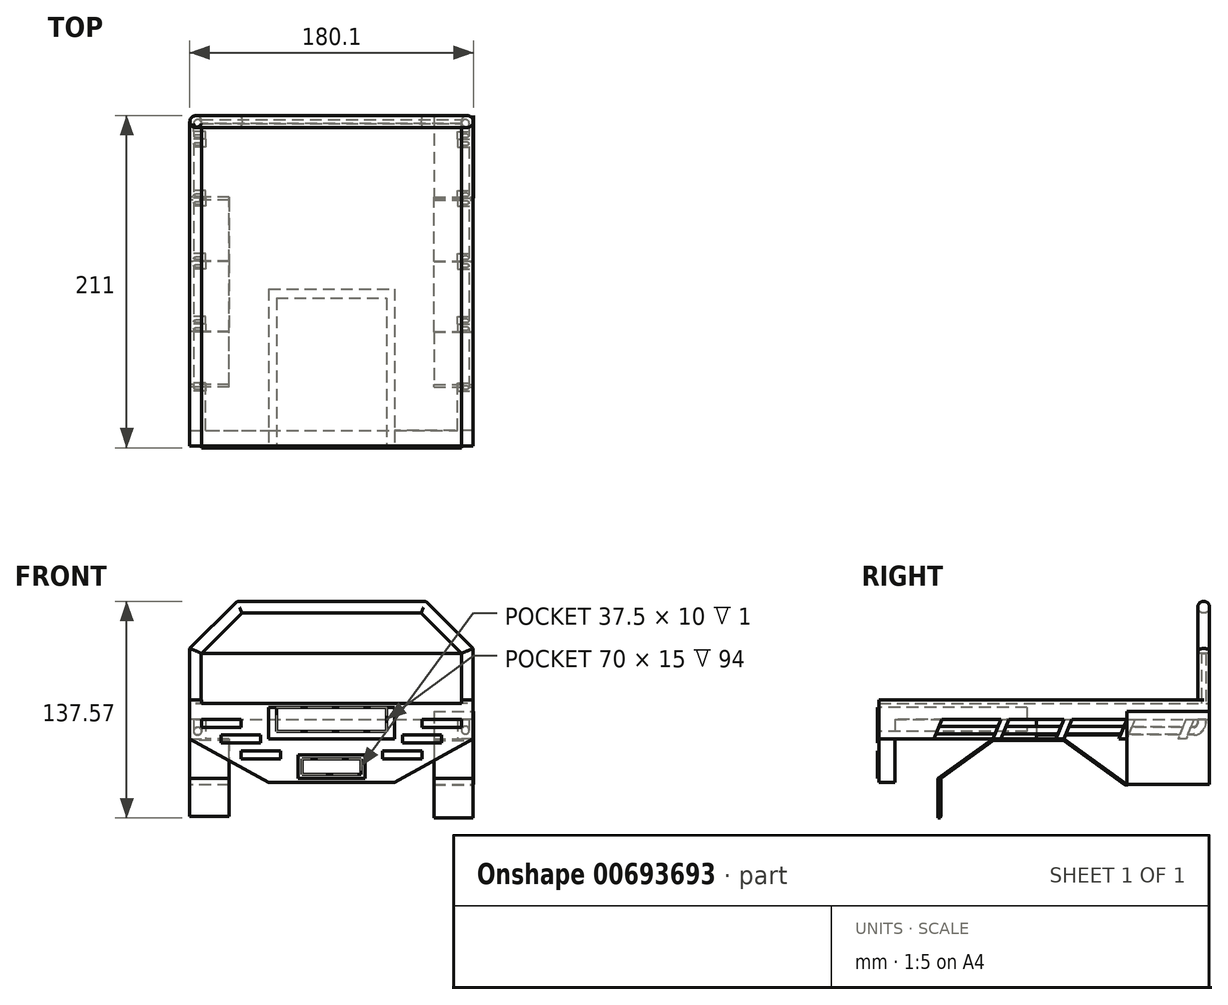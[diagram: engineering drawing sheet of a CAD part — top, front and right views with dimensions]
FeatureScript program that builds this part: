
annotation { "Feature Type Name" : "Feature", "Feature Type Description" : "" }
export const myFeature = defineFeature(function(context is Context, id is Id, definition is map)
    precondition{}
    {
        {
            var Q0;
            Q0=qCreatedBy(makeId("Top.planeOp"),FACE);
            var sketch = newSketch(context, id + "F0", { "sketchPlane" : qUnion([Q0])});
            skLineSegment(sketch, "E0.bottom", {"start": v(0, 0) * mm, "end": v(180, 0) * mm});
            skLineSegment(sketch, "E0.top", {"start": v(0, 210) * mm, "end": v(180, 210) * mm});
            skLineSegment(sketch, "E0.left", {"start": v(0, 0) * mm, "end": v(0, 210) * mm});
            skLineSegment(sketch, "E0.right", {"start": v(180, 0) * mm, "end": v(180, 210) * mm});
            skSolve(sketch);
        }
        {
            var Q0;
            Q0=qSketchRegion(id+"F0",true);
            extrude(context, id + "F1", {"entities" : qUnion([Q0]), "depth" : 10 * mm, "offsetDistance" : 25 * mm});
        }
        {
            var Q0;
            Q0=qCreatedBy(makeId("Front.planeOp"),FACE);
            cPlane(context, id + "F2", {"entities" : qUnion([Q0]), "cplaneType" : CPlaneType.OFFSET, "offset" : 210 * mm, "oppositeDirection" : true, "width" : 150 * mm, "height" : 150 * mm});
        }
        {
            var Q0;
            Q0=qCreatedBy(id+"F2.planeOp",FACE);
            var sketch = newSketch(context, id + "F3", { "sketchPlane" : qUnion([Q0])});
            skLineSegment(sketch, "E1.left", {"start": v(0, 10) * mm, "end": v(0, 45) * mm});
            skLineSegment(sketch, "E2.0", {"start": v(7.5, 10) * mm, "end": v(7.5, 41.9) * mm});
            skPoint(sketch, "E3", {"position": v(30, 75) * mm});
            skPoint(sketch, "E4", {"position": v(0, 45) * mm});
            skLineSegment(sketch, "E5", {"start": v(0, 45) * mm, "end": v(30, 75) * mm});
            skLineSegment(sketch, "E6.0", {"start": v(7.5, 41.9) * mm, "end": v(33.1, 67.5) * mm});
            skLineSegment(sketch, "E7.trimOffspring", {"start": v(33.1, 67.5) * mm, "end": v(105, 67.5) * mm});
            skLineSegment(sketch, "E8.trimOffspring", {"start": v(30, 75) * mm, "end": v(105, 75) * mm});
            skPoint(sketch, "E1.top.start.orphan", {"position": v(0, 75) * mm});
            skLineSegment(sketch, "E9.0", {"start": v(90, 0) * mm, "end": v(90, 45) * mm});
            skLineSegment(sketch, "E10.MirrorCS", {"start": v(180, 10) * mm, "end": v(180, 45) * mm});
            skLineSegment(sketch, "E11.MirrorCS", {"start": v(172.5, 10) * mm, "end": v(172.5, 41.9) * mm});
            skLineSegment(sketch, "E12.MirrorCS", {"start": v(172.5, 41.9) * mm, "end": v(146.9, 67.5) * mm});
            skLineSegment(sketch, "E13.MirrorCS", {"start": v(180, 45) * mm, "end": v(150, 75) * mm});
            skLineSegment(sketch, "E14.MirrorCS", {"start": v(146.9, 67.5) * mm, "end": v(75, 67.5) * mm});
            skLineSegment(sketch, "E15.MirrorCS", {"start": v(150, 75) * mm, "end": v(75, 75) * mm});
            skLineSegment(sketch, "E16.0", {"start": v(0, 10) * mm, "end": v(7.5, 10) * mm});
            skLineSegment(sketch, "E17.0", {"start": v(180, 10) * mm, "end": v(172.5, 10) * mm});
            skPoint(sketch, "E18.MirrorCS.end.orphan", {"position": v(172.5, 0) * mm});
            skPoint(sketch, "E18.MirrorCS.start.orphan", {"position": v(180, 0) * mm});
            skPoint(sketch, "E1.bottom.end.orphan", {"position": v(7.5, 0) * mm});
            skPoint(sketch, "E1.bottom.start.orphan", {"position": v(0, 0) * mm});
            skSolve(sketch);
        }
        {
            var Q0;
            Q0=qSketchRegion(id+"F3",true);
            extrude(context, id + "F4", {"entities" : qUnion([Q0]), "operationType" : NewBodyOperationType.ADD, "depth" : 7.5 * mm, "offsetDistance" : 25 * mm});
        }
        {
            var Q0;
            Q0=qCreatedBy(id+"F2.planeOp",FACE);
            cPlane(context, id + "F5", {"entities" : qUnion([Q0]), "cplaneType" : CPlaneType.OFFSET, "offset" : 2.5 * mm, "width" : 150 * mm, "height" : 150 * mm});
        }
        {
            var Q0;
            Q0=qCreatedBy(id+"F5.planeOp",FACE);
            var sketch = newSketch(context, id + "F6", { "sketchPlane" : qUnion([Q0])});
            skLineSegment(sketch, "E19.bottom", {"start": v(0, 0) * mm, "end": v(90, 0) * mm});
            skLineSegment(sketch, "E19.top", {"start": v(0, 41.85) * mm, "end": v(90, 41.85) * mm});
            skLineSegment(sketch, "E19.left", {"start": v(0, 0) * mm, "end": v(0, 41.85) * mm});
            skLineSegment(sketch, "E20.MirrorCS", {"start": v(180, 41.85) * mm, "end": v(90, 41.85) * mm});
            skLineSegment(sketch, "E21.MirrorCS", {"start": v(180, 0) * mm, "end": v(90, 0) * mm});
            skLineSegment(sketch, "E22.MirrorCS", {"start": v(180, 0) * mm, "end": v(180, 41.85) * mm});
            skSolve(sketch);
        }
        {
            var Q0;
            Q0=qSketchRegion(id+"F6",true);
            extrude(context, id + "F7", {"entities" : qUnion([Q0]), "operationType" : NewBodyOperationType.ADD, "depth" : 2.5 * mm, "offsetDistance" : 25 * mm});
        }
        {
            var Q0;
            Q0=qCreatedBy(makeId("Right.planeOp"),FACE);
            var sketch = newSketch(context, id + "F8", { "sketchPlane" : qUnion([Q0])});
            skLineSegment(sketch, "E23.bottom", {"start": v(0, 0) * mm, "end": v(205, 0) * mm});
            skLineSegment(sketch, "E23.top", {"start": v(0, 12.5) * mm, "end": v(205, 12.5) * mm});
            skLineSegment(sketch, "E23.left", {"start": v(0, 0) * mm, "end": v(0, 12.5) * mm});
            skLineSegment(sketch, "E23.right", {"start": v(205, 0) * mm, "end": v(205, 12.5) * mm});
            skSolve(sketch);
        }
        {
            var Q0;
            Q0=qSketchRegion(id+"F8",true);
            extrude(context, id + "F9", {"entities" : qUnion([Q0]), "operationType" : NewBodyOperationType.ADD, "depth" : 7.5 * mm, "offsetDistance" : 25 * mm});
        }
        {
            var Q0;
            Q0=makeQuery(id+"F4.boolean.opBoolean","MERGE",FACE,{"derivedFrom":[makeQuery(id+"F1.opExtrude","SWEPT_FACE",FACE,{"disambiguationData":[OSD([sQuery(id+"F0.wireOp",EDGE,"E0.right")])]}),makeQuery(id+"F4.opExtrude","SWEPT_FACE",FACE,{"disambiguationData":[OSD([sQuery(id+"F3.wireOp",EDGE,"E10.MirrorCS")])]})]});
            var sketch = newSketch(context, id + "F10", { "sketchPlane" : qUnion([Q0])});
            skLineSegment(sketch, "E24.bottom", {"start": v(0, 0) * mm, "end": v(205, 0) * mm});
            skLineSegment(sketch, "E24.top", {"start": v(0, 12.5) * mm, "end": v(205, 12.5) * mm});
            skLineSegment(sketch, "E24.left", {"start": v(0, 0) * mm, "end": v(0, 12.5) * mm});
            skLineSegment(sketch, "E24.right", {"start": v(205, 0) * mm, "end": v(205, 12.5) * mm});
            skSolve(sketch);
        }
        {
            var Q0;
            Q0=qSketchRegion(id+"F10",true);
            extrude(context, id + "F11", {"entities" : qUnion([Q0]), "operationType" : NewBodyOperationType.ADD, "oppositeDirection" : true, "depth" : 7.5 * mm, "offsetDistance" : 25 * mm});
        }
        {
            var Q0;
            Q0=qCreatedBy(makeId("Right.planeOp"),FACE);
            cPlane(context, id + "F12", {"entities" : qUnion([Q0]), "cplaneType" : CPlaneType.OFFSET, "offset" : 2.5 * mm, "width" : 150 * mm, "height" : 150 * mm});
        }
        {
            var Q0;
            Q0=qCreatedBy(makeId("Right.planeOp"),FACE);
            cPlane(context, id + "F13", {"entities" : qUnion([Q0]), "cplaneType" : CPlaneType.OFFSET, "offset" : 177.5 * mm, "width" : 150 * mm, "height" : 150 * mm});
        }
        {
            var Q0;
            Q0=qCreatedBy(id+"F12.planeOp",FACE);
            var sketch = newSketch(context, id + "F14", { "sketchPlane" : qUnion([Q0])});
            skLineSegment(sketch, "E25.top", {"start": v(0, -10) * mm, "end": v(200, -10) * mm});
            skLineSegment(sketch, "E26.0", {"start": v(207.5, 5) * mm, "end": v(207.5, -2.5) * mm});
            skArc(sketch, "E27", {"start": v(200, -10) * mm, "mid": v(205.3, -7.8) * mm, "end": v(207.5, -2.5) * mm});
            skPoint(sketch, "E28.orphan", {"position": v(207.5, -5) * mm});
            skLineSegment(sketch, "E29.0", {"start": v(0, -5) * mm, "end": v(200, -5) * mm});
            skArc(sketch, "E29.1", {"start": v(200, -5) * mm, "mid": v(201.77, -4.27) * mm, "end": v(202.5, -2.5) * mm});
            skLineSegment(sketch, "E29.2", {"start": v(202.5, 5) * mm, "end": v(202.5, -2.5) * mm});
            skLineSegment(sketch, "E30", {"start": v(207.5, 5) * mm, "end": v(202.5, 5) * mm});
            skLineSegment(sketch, "E31", {"start": v(0, -5) * mm, "end": v(0, -10) * mm});
            skLineSegment(sketch, "E32", {"start": v(207.5, 0) * mm, "end": v(202.5, 0) * mm});
            skSolve(sketch);
        }
        {
            var Q0;
            Q0=qSketchRegion(id+"F14",true);
            extrude(context, id + "F15", {"entities" : qUnion([Q0]), "operationType" : NewBodyOperationType.ADD, "depth" : 5 * mm, "offsetDistance" : 25 * mm});
        }
        {
            var Q0;
            Q0=makeQuery(id+"F15.opExtrude","CAP_EDGE",EDGE,{"disambiguationData":[OSD([sQuery(id+"F14.wireOp",EDGE,"E29.0")])],"isStart":true});
            var Q1;
            Q1=makeQuery(id+"F15.opExtrude","CAP_EDGE",EDGE,{"disambiguationData":[OSD([sQuery(id+"F14.wireOp",EDGE,"E25.top")])],"isStart":true});
            var Q2;
            Q2=makeQuery(id+"F15.opExtrude","CAP_EDGE",EDGE,{"disambiguationData":[OSD([sQuery(id+"F14.wireOp",EDGE,"E29.0")])],"isStart":false});
            var Q3;
            Q3=makeQuery(id+"F15.opExtrude","CAP_EDGE",EDGE,{"disambiguationData":[OSD([sQuery(id+"F14.wireOp",EDGE,"E25.top")])],"isStart":false});
            var Q4;
            Q4=makeQuery(id+"F15.opExtrude","CAP_EDGE",EDGE,{"disambiguationData":[OSD([sQuery(id+"F14.wireOp",EDGE,"E26.0")])],"isStart":false});
            var Q5;
            Q5=makeQuery(id+"F15.opExtrude","CAP_EDGE",EDGE,{"disambiguationData":[OSD([sQuery(id+"F14.wireOp",EDGE,"E29.2")])],"isStart":false});
            var Q6;
            Q6=makeQuery(id+"F15.opExtrude","CAP_EDGE",EDGE,{"disambiguationData":[OSD([sQuery(id+"F14.wireOp",EDGE,"E29.1")])],"isStart":false});
            var Q7;
            Q7=makeQuery(id+"F15.opExtrude","CAP_EDGE",EDGE,{"disambiguationData":[OSD([sQuery(id+"F14.wireOp",EDGE,"E27")])],"isStart":false});
            var Q8;
            Q8=makeQuery(id+"F15.opExtrude","CAP_EDGE",EDGE,{"disambiguationData":[OSD([sQuery(id+"F14.wireOp",EDGE,"E29.1")])],"isStart":true});
            var Q9;
            Q9=makeQuery(id+"F15.opExtrude","CAP_EDGE",EDGE,{"disambiguationData":[OSD([sQuery(id+"F14.wireOp",EDGE,"E29.2")])],"isStart":true});
            var Q10;
            Q10=makeQuery(id+"F15.opExtrude","CAP_EDGE",EDGE,{"disambiguationData":[OSD([sQuery(id+"F14.wireOp",EDGE,"E26.0")])],"isStart":true});
            var Q11;
            Q11=makeQuery(id+"F15.opExtrude","CAP_EDGE",EDGE,{"disambiguationData":[OSD([sQuery(id+"F14.wireOp",EDGE,"E27")])],"isStart":true});
            fillet(context, id + "F16", {"entities" : qUnion([Q0, Q1, Q2, Q3, Q4, Q5, Q6, Q7, Q8, Q9, Q10, Q11]), "radius" : 2.5 * mm, "tangentPropagation" : true, "allowEdgeOverflow" : false});
        }
        {
            var Q0;
            Q0=qCreatedBy(id+"F13.planeOp",FACE);
            var sketch = newSketch(context, id + "F17", { "sketchPlane" : qUnion([Q0])});
            skLineSegment(sketch, "E33.top", {"start": v(0, -9.36) * mm, "end": v(200, -9.36) * mm});
            skLineSegment(sketch, "E34.0", {"start": v(207.5, 5.64) * mm, "end": v(207.5, -1.86) * mm});
            skArc(sketch, "E35", {"start": v(200, -9.36) * mm, "mid": v(205.3, -7.17) * mm, "end": v(207.5, -1.86) * mm});
            skPoint(sketch, "E36.orphan", {"position": v(44.11, -1.86) * mm});
            skLineSegment(sketch, "E37.0", {"start": v(0, -4.36) * mm, "end": v(200, -4.36) * mm});
            skArc(sketch, "E37.1", {"start": v(200, -4.36) * mm, "mid": v(201.77, -3.63) * mm, "end": v(202.5, -1.86) * mm});
            skLineSegment(sketch, "E37.2", {"start": v(202.5, 5.64) * mm, "end": v(202.5, -1.86) * mm});
            skLineSegment(sketch, "E38", {"start": v(207.5, 5.64) * mm, "end": v(202.5, 5.64) * mm});
            skLineSegment(sketch, "E39", {"start": v(0, -4.36) * mm, "end": v(0, -9.36) * mm});
            skSolve(sketch);
        }
        {
            var Q0;
            Q0=qSketchRegion(id+"F17",true);
            extrude(context, id + "F18", {"entities" : qUnion([Q0]), "operationType" : NewBodyOperationType.ADD, "oppositeDirection" : true, "depth" : 5 * mm, "offsetDistance" : 25 * mm});
        }
        {
            var Q0;
            Q0=makeQuery(id+"F18.opExtrude","CAP_EDGE",EDGE,{"disambiguationData":[OSD([sQuery(id+"F17.wireOp",EDGE,"E37.2")])],"isStart":false});
            var Q1;
            Q1=makeQuery(id+"F18.opExtrude","CAP_EDGE",EDGE,{"disambiguationData":[OSD([sQuery(id+"F17.wireOp",EDGE,"E37.1")])],"isStart":false});
            var Q2;
            Q2=makeQuery(id+"F18.opExtrude","CAP_EDGE",EDGE,{"disambiguationData":[OSD([sQuery(id+"F17.wireOp",EDGE,"E37.0")])],"isStart":false});
            var Q3;
            Q3=makeQuery(id+"F18.opExtrude","CAP_EDGE",EDGE,{"disambiguationData":[OSD([sQuery(id+"F17.wireOp",EDGE,"E35")])],"isStart":false});
            var Q4;
            Q4=makeQuery(id+"F18.opExtrude","CAP_EDGE",EDGE,{"disambiguationData":[OSD([sQuery(id+"F17.wireOp",EDGE,"E34.0")])],"isStart":false});
            var Q5;
            Q5=makeQuery(id+"F18.opExtrude","CAP_EDGE",EDGE,{"disambiguationData":[OSD([sQuery(id+"F17.wireOp",EDGE,"E33.top")])],"isStart":false});
            var Q6;
            Q6=makeQuery(id+"F18.opExtrude","CAP_EDGE",EDGE,{"disambiguationData":[OSD([sQuery(id+"F17.wireOp",EDGE,"E37.0")])],"isStart":true});
            var Q7;
            Q7=makeQuery(id+"F18.opExtrude","CAP_EDGE",EDGE,{"disambiguationData":[OSD([sQuery(id+"F17.wireOp",EDGE,"E37.2")])],"isStart":true});
            var Q8;
            Q8=makeQuery(id+"F18.opExtrude","CAP_EDGE",EDGE,{"disambiguationData":[OSD([sQuery(id+"F17.wireOp",EDGE,"E37.1")])],"isStart":true});
            var Q9;
            Q9=makeQuery(id+"F18.opExtrude","CAP_EDGE",EDGE,{"disambiguationData":[OSD([sQuery(id+"F17.wireOp",EDGE,"E33.top")])],"isStart":true});
            var Q10;
            Q10=makeQuery(id+"F18.opExtrude","CAP_EDGE",EDGE,{"disambiguationData":[OSD([sQuery(id+"F17.wireOp",EDGE,"E35")])],"isStart":true});
            var Q11;
            Q11=makeQuery(id+"F18.opExtrude","CAP_EDGE",EDGE,{"disambiguationData":[OSD([sQuery(id+"F17.wireOp",EDGE,"E34.0")])],"isStart":true});
            fillet(context, id + "F19", {"entities" : qUnion([Q0, Q1, Q2, Q3, Q4, Q5, Q6, Q7, Q8, Q9, Q10, Q11]), "radius" : 2.5 * mm, "tangentPropagation" : true, "allowEdgeOverflow" : false});
        }
        {
            var Q0;
            Q0=qCreatedBy(makeId("Right.planeOp"),FACE);
            var sketch = newSketch(context, id + "F20", { "sketchPlane" : qUnion([Q0])});
            skLineSegment(sketch, "E40.bottom", {"start": v(0, 0) * mm, "end": v(40, 0) * mm});
            skLineSegment(sketch, "E40.top", {"start": v(0, -12.5) * mm, "end": v(35, -12.5) * mm});
            skLineSegment(sketch, "E40.left", {"start": v(0, 0) * mm, "end": v(0, -12.5) * mm});
            skPoint(sketch, "E41", {"position": v(35, -12.5) * mm});
            skPoint(sketch, "E42", {"position": v(40, 0) * mm});
            skLineSegment(sketch, "E43", {"start": v(40, 0) * mm, "end": v(35, -12.5) * mm});
            skLineSegment(sketch, "E44", {"start": v(200, 0) * mm, "end": v(195, -12.5) * mm});
            skLineSegment(sketch, "E45", {"start": v(195, 0) * mm, "end": v(190, -12.5) * mm});
            skLineSegment(sketch, "E46", {"start": v(82.5, 0) * mm, "end": v(77.5, -12.5) * mm});
            skLineSegment(sketch, "E47", {"start": v(77.5, 0) * mm, "end": v(72.5, -12.5) * mm});
            skLineSegment(sketch, "E48", {"start": v(122.5, 0) * mm, "end": v(117.5, -12.5) * mm});
            skLineSegment(sketch, "E49", {"start": v(117.5, 0) * mm, "end": v(112.5, -12.5) * mm});
            skLineSegment(sketch, "E50", {"start": v(162.5, 0) * mm, "end": v(157.5, -12.5) * mm});
            skLineSegment(sketch, "E51", {"start": v(157.5, 0) * mm, "end": v(152.5, -12.5) * mm});
            skLineSegment(sketch, "E52.trimOffspring", {"start": v(195, 0) * mm, "end": v(200, 0) * mm});
            skLineSegment(sketch, "E53.trimOffspring", {"start": v(157.5, 0) * mm, "end": v(162.5, 0) * mm});
            skLineSegment(sketch, "E54.trimOffspring", {"start": v(117.5, 0) * mm, "end": v(122.5, 0) * mm});
            skLineSegment(sketch, "E55.trimOffspring", {"start": v(112.5, -12.5) * mm, "end": v(117.5, -12.5) * mm});
            skLineSegment(sketch, "E56.trimOffspring", {"start": v(72.5, -12.5) * mm, "end": v(77.5, -12.5) * mm});
            skLineSegment(sketch, "E57.trimOffspring", {"start": v(77.5, 0) * mm, "end": v(82.5, 0) * mm});
            skLineSegment(sketch, "E58.top", {"start": v(195, -37.5) * mm, "end": v(152.5, -37.5) * mm});
            skLineSegment(sketch, "E58.left", {"start": v(195, -12.5) * mm, "end": v(195, -37.5) * mm});
            skLineSegment(sketch, "E59.0", {"start": v(190, -12.5) * mm, "end": v(190, -32.5) * mm});
            skLineSegment(sketch, "E59.1", {"start": v(190, -32.5) * mm, "end": v(157.5, -32.5) * mm});
            skLineSegment(sketch, "E60", {"start": v(195, -12.5) * mm, "end": v(190, -12.5) * mm});
            skLineSegment(sketch, "E61", {"start": v(157.5, -12.5) * mm, "end": v(152.5, -12.5) * mm});
            skSolve(sketch);
        }
        {
            var Q0;
            Q0=qSketchRegion(id+"F20",true);
            extrude(context, id + "F21", {"entities" : qUnion([Q0]), "operationType" : NewBodyOperationType.ADD, "depth" : 10 * mm, "offsetDistance" : 25 * mm});
        }
        {
            var Q0;
            Q0=qCreatedBy(makeId("Right.planeOp"),FACE);
            cPlane(context, id + "F22", {"entities" : qUnion([Q0]), "cplaneType" : CPlaneType.OFFSET, "offset" : 180 * mm, "width" : 150 * mm, "height" : 150 * mm});
        }
        {
            var Q0;
            Q0=qCreatedBy(id+"F22.planeOp",FACE);
            var sketch = newSketch(context, id + "F23", { "sketchPlane" : qUnion([Q0])});
            skLineSegment(sketch, "E62.bottom", {"start": v(0, 0) * mm, "end": v(40, 0) * mm});
            skLineSegment(sketch, "E62.top", {"start": v(0, -12.5) * mm, "end": v(35, -12.5) * mm});
            skLineSegment(sketch, "E62.left", {"start": v(0, 0) * mm, "end": v(0, -12.5) * mm});
            skPoint(sketch, "E63", {"position": v(-71.36, -6.25) * mm});
            skPoint(sketch, "E64", {"position": v(-66.36, 6.25) * mm});
            skLineSegment(sketch, "E65", {"start": v(40, 0) * mm, "end": v(35, -12.5) * mm});
            skLineSegment(sketch, "E66", {"start": v(200, 0) * mm, "end": v(195, -12.5) * mm});
            skLineSegment(sketch, "E67", {"start": v(195, 0) * mm, "end": v(190, -12.5) * mm});
            skLineSegment(sketch, "E68", {"start": v(82.5, 0) * mm, "end": v(77.5, -12.5) * mm});
            skLineSegment(sketch, "E69", {"start": v(77.5, 0) * mm, "end": v(72.5, -12.5) * mm});
            skLineSegment(sketch, "E70", {"start": v(122.5, 0) * mm, "end": v(117.5, -12.5) * mm});
            skLineSegment(sketch, "E71", {"start": v(117.5, 0) * mm, "end": v(112.5, -12.5) * mm});
            skLineSegment(sketch, "E72", {"start": v(162.5, 0) * mm, "end": v(157.5, -12.5) * mm});
            skLineSegment(sketch, "E73", {"start": v(157.5, 0) * mm, "end": v(152.5, -12.5) * mm});
            skLineSegment(sketch, "E74.trimOffspring", {"start": v(195, 0) * mm, "end": v(200, 0) * mm});
            skLineSegment(sketch, "E75.trimOffspring", {"start": v(157.5, 0) * mm, "end": v(162.5, 0) * mm});
            skLineSegment(sketch, "E76.trimOffspring", {"start": v(117.5, 0) * mm, "end": v(122.5, 0) * mm});
            skLineSegment(sketch, "E77.trimOffspring", {"start": v(112.5, -12.5) * mm, "end": v(117.5, -12.5) * mm});
            skLineSegment(sketch, "E78.trimOffspring", {"start": v(72.5, -12.5) * mm, "end": v(77.5, -12.5) * mm});
            skLineSegment(sketch, "E79.trimOffspring", {"start": v(77.5, 0) * mm, "end": v(82.5, 0) * mm});
            skLineSegment(sketch, "E80.0", {"start": v(0, 5) * mm, "end": v(40, 5) * mm});
            skLineSegment(sketch, "E81.0", {"start": v(77.5, 5) * mm, "end": v(82.5, 5) * mm});
            skLineSegment(sketch, "E82.0", {"start": v(117.5, 5) * mm, "end": v(122.5, 5) * mm});
            skLineSegment(sketch, "E83.0", {"start": v(157.5, 5) * mm, "end": v(162.5, 5) * mm});
            skLineSegment(sketch, "E84.0", {"start": v(195, 5) * mm, "end": v(200, 5) * mm});
            skLineSegment(sketch, "E85", {"start": v(0, 5) * mm, "end": v(0, 0) * mm});
            skLineSegment(sketch, "E86", {"start": v(40, 0) * mm, "end": v(40, 5) * mm});
            skLineSegment(sketch, "E87", {"start": v(77.5, 0) * mm, "end": v(77.5, 5) * mm});
            skLineSegment(sketch, "E88", {"start": v(82.5, 0) * mm, "end": v(82.5, 5) * mm});
            skLineSegment(sketch, "E89", {"start": v(117.5, 0) * mm, "end": v(117.5, 5) * mm});
            skLineSegment(sketch, "E90", {"start": v(122.5, 0) * mm, "end": v(122.5, 5) * mm});
            skLineSegment(sketch, "E91", {"start": v(157.5, 0) * mm, "end": v(157.5, 5) * mm});
            skLineSegment(sketch, "E92", {"start": v(162.5, 0) * mm, "end": v(162.5, 5) * mm});
            skLineSegment(sketch, "E93", {"start": v(195, 0) * mm, "end": v(195, 5) * mm});
            skLineSegment(sketch, "E94", {"start": v(200, 0) * mm, "end": v(200, 5) * mm});
            skLineSegment(sketch, "E95", {"start": v(152.5, -12.5) * mm, "end": v(157.5, -12.5) * mm});
            skLineSegment(sketch, "E96", {"start": v(190, -12.5) * mm, "end": v(195, -12.5) * mm});
            skSolve(sketch);
        }
        {
            var Q0;
            Q0=qSketchRegion(id+"F23",true);
            var Q1;
            Q1=makeQuery(id+"F21.opExtrude","CAP_FACE",FACE,{"disambiguationData":[OSD([sQuery(id+"F20.wireOp",EDGE,"E44"),sQuery(id+"F20.wireOp",EDGE,"E45"),sQuery(id+"F20.wireOp",EDGE,"E52.trimOffspring"),sQuery(id+"F20.wireOp",EDGE,"E60")])],"isStart":false});
            extrude(context, id + "F24", {"entities" : qUnion([Q0, Q1]), "operationType" : NewBodyOperationType.ADD, "oppositeDirection" : true, "depth" : 10 * mm, "offsetDistance" : 25 * mm});
        }
        {
            var Q0;
            Q0=qCreatedBy(makeId("Front.planeOp"),FACE);
            var sketch = newSketch(context, id + "F25", { "sketchPlane" : qUnion([Q0])});
            skLineSegment(sketch, "E97.bottom", {"start": v(0, 0) * mm, "end": v(90, 0) * mm});
            skLineSegment(sketch, "E97.top", {"start": v(50, -40) * mm, "end": v(90, -40) * mm});
            skLineSegment(sketch, "E97.left", {"start": v(0, 0) * mm, "end": v(0, -12.5) * mm});
            skPoint(sketch, "E98", {"position": v(50, -40) * mm});
            skPoint(sketch, "E99", {"position": v(0, -12.5) * mm});
            skLineSegment(sketch, "E100", {"start": v(0, -12.5) * mm, "end": v(50, -40) * mm});
            skPoint(sketch, "E101.orphan", {"position": v(0, -40) * mm});
            skLineSegment(sketch, "E102.MirrorCS", {"start": v(180, 0) * mm, "end": v(90, 0) * mm});
            skLineSegment(sketch, "E103.MirrorCS", {"start": v(180, 0) * mm, "end": v(180, -12.5) * mm});
            skLineSegment(sketch, "E104.MirrorCS", {"start": v(180, -12.5) * mm, "end": v(130, -40) * mm});
            skLineSegment(sketch, "E105.MirrorCS", {"start": v(130, -40) * mm, "end": v(90, -40) * mm});
            skSolve(sketch);
        }
        {
            var Q0;
            Q0=qSketchRegion(id+"F25",true);
            extrude(context, id + "F26", {"entities" : qUnion([Q0]), "operationType" : NewBodyOperationType.ADD, "oppositeDirection" : true, "depth" : 10 * mm, "offsetDistance" : 25 * mm});
        }
        {
            var Q0;
            Q0=qCreatedBy(makeId("Front.planeOp"),FACE);
            var sketch = newSketch(context, id + "F27", { "sketchPlane" : qUnion([Q0])});
            skLineSegment(sketch, "E106.0", {"start": v(71.25, -25) * mm, "end": v(71.25, -35) * mm});
            skLineSegment(sketch, "E107.0", {"start": v(108.75, -25) * mm, "end": v(108.75, -35) * mm});
            skLineSegment(sketch, "E108.0", {"start": v(71.25, -35) * mm, "end": v(108.75, -35) * mm});
            skLineSegment(sketch, "E109.0", {"start": v(71.25, -25) * mm, "end": v(108.75, -25) * mm});
            skLineSegment(sketch, "E110.0", {"start": v(68.75, -22.5) * mm, "end": v(111.25, -22.5) * mm});
            skLineSegment(sketch, "E110.1", {"start": v(68.75, -22.5) * mm, "end": v(68.75, -37.5) * mm});
            skLineSegment(sketch, "E110.2", {"start": v(68.75, -37.5) * mm, "end": v(111.25, -37.5) * mm});
            skLineSegment(sketch, "E110.3", {"start": v(111.25, -22.5) * mm, "end": v(111.25, -37.5) * mm});
            skSolve(sketch);
        }
        {
            var Q0;
            Q0=qSketchRegion(id+"F27",true);
            extrude(context, id + "F28", {"entities" : qUnion([Q0]), "operationType" : NewBodyOperationType.ADD, "depth" : 1 * mm, "offsetDistance" : 25 * mm});
        }
        {
            var Q0;
            Q0=qCreatedBy(makeId("Front.planeOp"),FACE);
            var sketch = newSketch(context, id + "F29", { "sketchPlane" : qUnion([Q0])});
            skLineSegment(sketch, "E111", {"start": v(50, 7.5) * mm, "end": v(50, -12.5) * mm});
            skLineSegment(sketch, "E112.0", {"start": v(130, 7.5) * mm, "end": v(130, -12.5) * mm});
            skLineSegment(sketch, "E113.0", {"start": v(50, 7.5) * mm, "end": v(130, 7.5) * mm});
            skLineSegment(sketch, "E114.0", {"start": v(50, -12.5) * mm, "end": v(130, -12.5) * mm});
            skSolve(sketch);
        }
        {
            var Q0;
            Q0=qSketchRegion(id+"F29",true);
            extrude(context, id + "F30", {"entities" : qUnion([Q0]), "operationType" : NewBodyOperationType.ADD, "oppositeDirection" : true, "depth" : 100 * mm, "offsetDistance" : 25 * mm, "hasSecondDirection" : true, "secondDirectionOppositeDirection" : false, "secondDirectionDepth" : 1 * mm});
        }
        {
            var Q0;
            Q0=qCreatedBy(makeId("Right.planeOp"),FACE);
            var sketch = newSketch(context, id + "F31", { "sketchPlane" : qUnion([Q0])});
            skLineSegment(sketch, "E115", {"start": v(152.5, -37.57) * mm, "end": v(117.5, -12.5) * mm});
            skLineSegment(sketch, "E116", {"start": v(152.5, -37.57) * mm, "end": v(158.15, -41.62) * mm});
            skLineSegment(sketch, "E117", {"start": v(117.5, -12.5) * mm, "end": v(95, -12.5) * mm});
            skPoint(sketch, "E118", {"position": v(95, -12.5) * mm});
            skPoint(sketch, "E119.orphan", {"position": v(72.5, -12.5) * mm});
            skLineSegment(sketch, "E120.MirrorCS", {"start": v(37.5, -37.57) * mm, "end": v(72.5, -12.5) * mm});
            skLineSegment(sketch, "E121.MirrorCS", {"start": v(72.5, -12.5) * mm, "end": v(95, -12.5) * mm});
            skLineSegment(sketch, "E122.0", {"start": v(151.92, -38.39) * mm, "end": v(156.43, -41.62) * mm});
            skLineSegment(sketch, "E122.1", {"start": v(39.22, -37.57) * mm, "end": v(72.82, -13.5) * mm});
            skLineSegment(sketch, "E122.2", {"start": v(72.82, -13.5) * mm, "end": v(95, -13.5) * mm});
            skLineSegment(sketch, "E122.3", {"start": v(117.18, -13.5) * mm, "end": v(95, -13.5) * mm});
            skLineSegment(sketch, "E122.4", {"start": v(151.92, -38.39) * mm, "end": v(117.18, -13.5) * mm});
            skLineSegment(sketch, "E123", {"start": v(158.15, -41.62) * mm, "end": v(156.43, -41.62) * mm});
            skLineSegment(sketch, "E124", {"start": v(39.22, -37.57) * mm, "end": v(39.22, -61.57) * mm});
            skLineSegment(sketch, "E125", {"start": v(37.5, -37.57) * mm, "end": v(37.5, -61.57) * mm});
            skLineSegment(sketch, "E126", {"start": v(37.5, -61.57) * mm, "end": v(39.22, -61.57) * mm});
            skPoint(sketch, "E127.start.orphan", {"position": v(122.5, 0) * mm});
            skLineSegment(sketch, "E128", {"start": v(0, 0) * mm, "end": v(0, -12.5) * mm});
            skSolve(sketch);
        }
        {
            var Q0;
            Q0=qSketchRegion(id+"F31",true);
            extrude(context, id + "F32", {"entities" : qUnion([Q0]), "operationType" : NewBodyOperationType.ADD, "depth" : 25 * mm, "offsetDistance" : 25 * mm});
        }
        {
            var Q0;
            Q0=makeQuery(id+"F30.opExtrude","CAP_FACE",FACE,{"disambiguationData":[OSD([sQuery(id+"F29.wireOp",EDGE,"E111"),sQuery(id+"F29.wireOp",EDGE,"E112.0"),sQuery(id+"F29.wireOp",EDGE,"E113.0"),sQuery(id+"F29.wireOp",EDGE,"E114.0")])],"isStart":true});
            var sketch = newSketch(context, id + "F33", { "sketchPlane" : qUnion([Q0])});
            skLineSegment(sketch, "E129.0", {"start": v(125, 7.5) * mm, "end": v(125, -7.5) * mm});
            skLineSegment(sketch, "E129.1", {"start": v(55, -7.5) * mm, "end": v(125, -7.5) * mm});
            skLineSegment(sketch, "E129.2", {"start": v(55, 7.5) * mm, "end": v(55, -7.5) * mm});
            skLineSegment(sketch, "E130", {"start": v(55, 7.5) * mm, "end": v(125, 7.5) * mm});
            skSolve(sketch);
        }
        {
            var Q0;
            Q0=qSketchRegion(id+"F33",true);
            extrude(context, id + "F34", {"entities" : qUnion([Q0]), "operationType" : NewBodyOperationType.REMOVE, "oppositeDirection" : true, "depth" : 95 * mm, "offsetDistance" : 25 * mm});
        }
        {
            var Q0;
            {var subQ0=sQuery(id+"F25.wireOp",EDGE,"E105.MirrorCS");var subQ1=sQuery(id+"F25.wireOp",EDGE,"E97.top");var subQ3=sQuery(id+"F0.wireOp",EDGE,"E0.left");var subQ4=sQuery(id+"F0.wireOp",EDGE,"E0.bottom");var subQ5=sQuery(id+"F23.wireOp",EDGE,"E85");var subQ6=sQuery(id+"F23.wireOp",EDGE,"E62.left");var subQ9=sQuery(id+"F8.wireOp",EDGE,"E23.left");var subQ13=sQuery(id+"F10.wireOp",EDGE,"E24.left");var subQ15=sQuery(id+"F20.wireOp",EDGE,"E40.left");var subQ16=sQuery(id+"F25.wireOp",EDGE,"E100");var subQ17=sQuery(id+"F25.wireOp",EDGE,"E104.MirrorCS");Q0=makeQuery(id+"F28.boolean.opBoolean","SPLIT",FACE,{"disambiguationData":[TD([makeQuery(id+"F1.opExtrude","SWEPT_FACE",FACE,{"disambiguationData":[OSD([subQ3])]})])],"derivedFrom":makeQuery(id+"F26.boolean.opBoolean","MERGE",FACE,{"derivedFrom":[makeQuery(id+"F24.boolean.opBoolean","MERGE",FACE,{"derivedFrom":[makeQuery(id+"F18.opExtrude","SWEPT_FACE",FACE,{"disambiguationData":[OSD([sQuery(id+"F17.wireOp",EDGE,"E39")])]}),makeQuery(id+"F21.boolean.opBoolean","MERGE",FACE,{"derivedFrom":[makeQuery(id+"F11.boolean.opBoolean","MERGE",FACE,{"derivedFrom":[makeQuery(id+"F9.boolean.opBoolean","MERGE",FACE,{"derivedFrom":[makeQuery(id+"F1.opExtrude","SWEPT_FACE",FACE,{"disambiguationData":[OSD([subQ4])]}),makeQuery(id+"F9.opExtrude","SWEPT_FACE",FACE,{"disambiguationData":[OSD([subQ9])]})]}),makeQuery(id+"F11.opExtrude","SWEPT_FACE",FACE,{"disambiguationData":[OSD([subQ13])]})]}),makeQuery(id+"F15.opExtrude","SWEPT_FACE",FACE,{"disambiguationData":[OSD([sQuery(id+"F14.wireOp",EDGE,"E31")])]}),makeQuery(id+"F21.opExtrude","SWEPT_FACE",FACE,{"disambiguationData":[OSD([subQ15])]})]}),makeQuery(id+"F24.opExtrude","SWEPT_FACE",FACE,{"disambiguationData":[OSD([subQ6,subQ5])]})]}),makeQuery(id+"F26.opExtrude","CAP_FACE",FACE,{"disambiguationData":[OSD([sQuery(id+"F25.wireOp",EDGE,"E97.bottom"),subQ1,sQuery(id+"F25.wireOp",EDGE,"E97.left"),subQ16,sQuery(id+"F25.wireOp",EDGE,"E102.MirrorCS"),sQuery(id+"F25.wireOp",EDGE,"E103.MirrorCS"),subQ17,subQ0])],"isStart":true})]})});}
            var sketch = newSketch(context, id + "F35", { "sketchPlane" : qUnion([Q0])});
            skLineSegment(sketch, "E131", {"start": v(7.5, 0) * mm, "end": v(32.5, 0) * mm});
            skLineSegment(sketch, "E132.0", {"start": v(7.5, 0) * mm, "end": v(7.5, -5) * mm});
            skLineSegment(sketch, "E133.0", {"start": v(7.5, -5) * mm, "end": v(32.5, -5) * mm});
            skLineSegment(sketch, "E134", {"start": v(32.5, -5) * mm, "end": v(32.5, 0) * mm});
            skPoint(sketch, "E135", {"position": v(20, 0) * mm});
            skLineSegment(sketch, "E136", {"start": v(20, -10) * mm, "end": v(20, -15) * mm});
            skLineSegment(sketch, "E137.0", {"start": v(45, -10) * mm, "end": v(45, -15) * mm});
            skLineSegment(sketch, "E138.0", {"start": v(20, -10) * mm, "end": v(45, -10) * mm});
            skLineSegment(sketch, "E139.0", {"start": v(20, -15) * mm, "end": v(45, -15) * mm});
            skLineSegment(sketch, "E140.0", {"start": v(32.5, -20) * mm, "end": v(57.5, -20) * mm});
            skLineSegment(sketch, "E141.0", {"start": v(32.5, -25) * mm, "end": v(57.5, -25) * mm});
            skLineSegment(sketch, "E142.0", {"start": v(57.5, -20) * mm, "end": v(57.5, -25) * mm});
            skLineSegment(sketch, "E143.trimOffspring", {"start": v(32.5, -20) * mm, "end": v(32.5, -25) * mm});
            skLineSegment(sketch, "E144.MirrorCS", {"start": v(147.5, -20) * mm, "end": v(122.5, -20) * mm});
            skLineSegment(sketch, "E145.MirrorCS", {"start": v(122.5, -20) * mm, "end": v(122.5, -25) * mm});
            skLineSegment(sketch, "E146.MirrorCS", {"start": v(147.5, -20) * mm, "end": v(147.5, -25) * mm});
            skLineSegment(sketch, "E147.MirrorCS", {"start": v(147.5, -25) * mm, "end": v(122.5, -25) * mm});
            skLineSegment(sketch, "E148.MirrorCS", {"start": v(160, -10) * mm, "end": v(135, -10) * mm});
            skLineSegment(sketch, "E149.MirrorCS", {"start": v(160, -10) * mm, "end": v(160, -15) * mm});
            skLineSegment(sketch, "E150.MirrorCS", {"start": v(135, -10) * mm, "end": v(135, -15) * mm});
            skLineSegment(sketch, "E151.MirrorCS", {"start": v(160, -15) * mm, "end": v(135, -15) * mm});
            skLineSegment(sketch, "E152.MirrorCS", {"start": v(172.5, 0) * mm, "end": v(147.5, 0) * mm});
            skLineSegment(sketch, "E153.MirrorCS", {"start": v(147.5, -5) * mm, "end": v(147.5, 0) * mm});
            skLineSegment(sketch, "E154.MirrorCS", {"start": v(172.5, 0) * mm, "end": v(172.5, -5) * mm});
            skLineSegment(sketch, "E155.MirrorCS", {"start": v(172.5, -5) * mm, "end": v(147.5, -5) * mm});
            skPoint(sketch, "E156.MirrorP", {"position": v(160, 0) * mm});
            skSolve(sketch);
        }
        {
            var Q0;
            Q0=qSketchRegion(id+"F35",true);
            extrude(context, id + "F36", {"entities" : qUnion([Q0]), "operationType" : NewBodyOperationType.ADD, "depth" : 1 * mm, "offsetDistance" : 25 * mm});
        }
        {
            var Q0;
            Q0=makeQuery(id+"F24.boolean.opBoolean","MERGE",FACE,{"derivedFrom":[makeQuery(id+"F11.boolean.opBoolean","MERGE",FACE,{"derivedFrom":[makeQuery(id+"F4.boolean.opBoolean","MERGE",FACE,{"derivedFrom":[makeQuery(id+"F1.opExtrude","SWEPT_FACE",FACE,{"disambiguationData":[OSD([sQuery(id+"F0.wireOp",EDGE,"E0.right")])]}),makeQuery(id+"F4.opExtrude","SWEPT_FACE",FACE,{"disambiguationData":[OSD([sQuery(id+"F3.wireOp",EDGE,"E10.MirrorCS")])]})]}),makeQuery(id+"F11.opExtrude","CAP_FACE",FACE,{"disambiguationData":[OSD([sQuery(id+"F10.wireOp",EDGE,"E24.bottom"),sQuery(id+"F10.wireOp",EDGE,"E24.top"),sQuery(id+"F10.wireOp",EDGE,"E24.left"),sQuery(id+"F10.wireOp",EDGE,"E24.right")])],"isStart":true})]}),makeQuery(id+"F24.opExtrude","CAP_FACE",FACE,{"disambiguationData":[OSD([sQuery(id+"F23.wireOp",EDGE,"E62.top"),sQuery(id+"F23.wireOp",EDGE,"E62.left"),sQuery(id+"F23.wireOp",EDGE,"E65"),sQuery(id+"F23.wireOp",EDGE,"E80.0"),sQuery(id+"F23.wireOp",EDGE,"E85"),sQuery(id+"F23.wireOp",EDGE,"E86")])],"isStart":true}),makeQuery(id+"F24.opExtrude","CAP_FACE",FACE,{"disambiguationData":[OSD([sQuery(id+"F23.wireOp",EDGE,"E66"),sQuery(id+"F23.wireOp",EDGE,"E67"),sQuery(id+"F23.wireOp",EDGE,"E72"),sQuery(id+"F23.wireOp",EDGE,"E73"),sQuery(id+"F23.wireOp",EDGE,"E83.0"),sQuery(id+"F23.wireOp",EDGE,"E84.0"),sQuery(id+"F23.wireOp",EDGE,"E91"),sQuery(id+"F23.wireOp",EDGE,"E92"),sQuery(id+"F23.wireOp",EDGE,"E93"),sQuery(id+"F23.wireOp",EDGE,"E94"),sQuery(id+"F23.wireOp",EDGE,"j2wuKbWy-859N-9TrD-dwRU-jK9p1SD8Web2.top"),sQuery(id+"F23.wireOp",EDGE,"j2wuKbWy-859N-9TrD-dwRU-jK9p1SD8Web2.left"),sQuery(id+"F23.wireOp",EDGE,"j2wuKbWy-859N-9TrD-dwRU-jK9p1SD8Web2.right"),sQuery(id+"F23.wireOp",EDGE,"db74b8e5-f1bc-416b-96d4-5efc23300016.0"),sQuery(id+"F23.wireOp",EDGE,"db74b8e5-f1bc-416b-96d4-5efc23300016.1"),sQuery(id+"F23.wireOp",EDGE,"db74b8e5-f1bc-416b-96d4-5efc23300016.2")])],"isStart":true}),makeQuery(id+"F24.opExtrude","CAP_FACE",FACE,{"disambiguationData":[OSD([sQuery(id+"F23.wireOp",EDGE,"E68"),sQuery(id+"F23.wireOp",EDGE,"E69"),sQuery(id+"F23.wireOp",EDGE,"E78.trimOffspring"),sQuery(id+"F23.wireOp",EDGE,"E81.0"),sQuery(id+"F23.wireOp",EDGE,"E87"),sQuery(id+"F23.wireOp",EDGE,"E88")])],"isStart":true}),makeQuery(id+"F24.opExtrude","CAP_FACE",FACE,{"disambiguationData":[OSD([sQuery(id+"F23.wireOp",EDGE,"E70"),sQuery(id+"F23.wireOp",EDGE,"E71"),sQuery(id+"F23.wireOp",EDGE,"E77.trimOffspring"),sQuery(id+"F23.wireOp",EDGE,"E82.0"),sQuery(id+"F23.wireOp",EDGE,"E89"),sQuery(id+"F23.wireOp",EDGE,"E90")])],"isStart":true})]});
            var sketch = newSketch(context, id + "F37", { "sketchPlane" : qUnion([Q0])});
            skLineSegment(sketch, "E157", {"start": v(72.5, -12.5) * mm, "end": v(117.5, -12.5) * mm});
            skLineSegment(sketch, "E158", {"start": v(117.5, -12.5) * mm, "end": v(158.15, -41.62) * mm});
            skLineSegment(sketch, "E159", {"start": v(72.5, -12.5) * mm, "end": v(37.5, -37.57) * mm});
            skLineSegment(sketch, "E160.0", {"start": v(72.82, -13.5) * mm, "end": v(39.14, -37.63) * mm});
            skLineSegment(sketch, "E160.1", {"start": v(72.82, -13.5) * mm, "end": v(117.18, -13.5) * mm});
            skLineSegment(sketch, "E160.2", {"start": v(117.18, -13.5) * mm, "end": v(156.35, -41.56) * mm});
            skLineSegment(sketch, "E161.trimOffspring", {"start": v(156.35, -41.56) * mm, "end": v(158.15, -41.62) * mm});
            skLineSegment(sketch, "E162", {"start": v(37.5, -37.57) * mm, "end": v(37.5, -62.57) * mm});
            skLineSegment(sketch, "E163", {"start": v(39.14, -37.63) * mm, "end": v(39.14, -62.57) * mm});
            skLineSegment(sketch, "E164", {"start": v(37.5, -62.57) * mm, "end": v(39.14, -62.57) * mm});
            skSolve(sketch);
        }
        {
            var Q0;
            Q0=qSketchRegion(id+"F37",true);
            extrude(context, id + "F38", {"entities" : qUnion([Q0]), "oppositeDirection" : true, "depth" : 25 * mm, "offsetDistance" : 25 * mm});
        }
        {
            var Q0;
            Q0=makeQuery(id+"F4.opExtrude","CAP_EDGE",EDGE,{"disambiguationData":[OSD([sQuery(id+"F3.wireOp",EDGE,"E5")])],"isStart":false});
            var Q1;
            Q1=makeQuery(id+"F4.opExtrude","CAP_EDGE",EDGE,{"disambiguationData":[OSD([sQuery(id+"F3.wireOp",EDGE,"E1.left")])],"isStart":false});
            var Q2;
            Q2=makeQuery(id+"F4.opExtrude","CAP_EDGE",EDGE,{"disambiguationData":[OSD([sQuery(id+"F3.wireOp",EDGE,"E6.0")])],"isStart":false});
            var Q3;
            Q3=makeQuery(id+"F4.opExtrude","CAP_EDGE",EDGE,{"disambiguationData":[OSD([sQuery(id+"F3.wireOp",EDGE,"E2.0")])],"isStart":false});
            var Q4;
            Q4=makeQuery(id+"F4.opExtrude","CAP_EDGE",EDGE,{"disambiguationData":[OSD([sQuery(id+"F3.wireOp",EDGE,"E5")])],"isStart":true});
            var Q5;
            Q5=makeQuery(id+"F4.boolean.opBoolean","MERGE",EDGE,{"derivedFrom":[makeQuery(id+"F1.opExtrude","SWEPT_EDGE",EDGE,{"disambiguationData":[OSD([sQuery(id+"F0.wireOp",EDGE,"E0.top"),sQuery(id+"F0.wireOp",EDGE,"E0.left")])]}),makeQuery(id+"F4.opExtrude","CAP_EDGE",EDGE,{"disambiguationData":[OSD([sQuery(id+"F3.wireOp",EDGE,"E1.left")])],"isStart":true})]});
            var Q6;
            Q6=makeQuery(id+"F4.opExtrude","CAP_EDGE",EDGE,{"disambiguationData":[OSD([sQuery(id+"F3.wireOp",EDGE,"E2.0")])],"isStart":true});
            var Q7;
            Q7=makeQuery(id+"F4.opExtrude","CAP_EDGE",EDGE,{"disambiguationData":[OSD([sQuery(id+"F3.wireOp",EDGE,"E6.0")])],"isStart":true});
            var Q8;
            Q8=makeQuery(id+"F4.opExtrude","CAP_EDGE",EDGE,{"disambiguationData":[OSD([sQuery(id+"F3.wireOp",EDGE,"E7.trimOffspring"),sQuery(id+"F3.wireOp",EDGE,"E14.MirrorCS")])],"isStart":true});
            var Q9;
            Q9=makeQuery(id+"F4.opExtrude","SWEPT_FACE",FACE,{"disambiguationData":[OSD([sQuery(id+"F3.wireOp",EDGE,"E8.trimOffspring"),sQuery(id+"F3.wireOp",EDGE,"E15.MirrorCS")])]});
            var Q10;
            Q10=makeQuery(id+"F4.opExtrude","CAP_EDGE",EDGE,{"disambiguationData":[OSD([sQuery(id+"F3.wireOp",EDGE,"E7.trimOffspring"),sQuery(id+"F3.wireOp",EDGE,"E14.MirrorCS")])],"isStart":false});
            var Q11;
            Q11=makeQuery(id+"F4.opExtrude","CAP_EDGE",EDGE,{"disambiguationData":[OSD([sQuery(id+"F3.wireOp",EDGE,"E8.trimOffspring"),sQuery(id+"F3.wireOp",EDGE,"E15.MirrorCS")])],"isStart":true});
            var Q12;
            Q12=makeQuery(id+"F4.opExtrude","CAP_EDGE",EDGE,{"disambiguationData":[OSD([sQuery(id+"F3.wireOp",EDGE,"E12.MirrorCS")])],"isStart":false});
            var Q13;
            Q13=makeQuery(id+"F4.opExtrude","CAP_EDGE",EDGE,{"disambiguationData":[OSD([sQuery(id+"F3.wireOp",EDGE,"E13.MirrorCS")])],"isStart":false});
            var Q14;
            Q14=makeQuery(id+"F4.opExtrude","CAP_EDGE",EDGE,{"disambiguationData":[OSD([sQuery(id+"F3.wireOp",EDGE,"E11.MirrorCS")])],"isStart":false});
            var Q15;
            Q15=makeQuery(id+"F4.opExtrude","CAP_EDGE",EDGE,{"disambiguationData":[OSD([sQuery(id+"F3.wireOp",EDGE,"E10.MirrorCS")])],"isStart":false});
            var Q16;
            Q16=makeQuery(id+"F4.boolean.opBoolean","MERGE",EDGE,{"derivedFrom":[makeQuery(id+"F1.opExtrude","SWEPT_EDGE",EDGE,{"disambiguationData":[OSD([sQuery(id+"F0.wireOp",EDGE,"E0.top"),sQuery(id+"F0.wireOp",EDGE,"E0.right")])]}),makeQuery(id+"F4.opExtrude","CAP_EDGE",EDGE,{"disambiguationData":[OSD([sQuery(id+"F3.wireOp",EDGE,"E10.MirrorCS")])],"isStart":true})]});
            var Q17;
            Q17=makeQuery(id+"F4.opExtrude","CAP_EDGE",EDGE,{"disambiguationData":[OSD([sQuery(id+"F3.wireOp",EDGE,"E13.MirrorCS")])],"isStart":true});
            var Q18;
            Q18=makeQuery(id+"F4.opExtrude","CAP_EDGE",EDGE,{"disambiguationData":[OSD([sQuery(id+"F3.wireOp",EDGE,"E11.MirrorCS")])],"isStart":true});
            var Q19;
            Q19=makeQuery(id+"F4.opExtrude","CAP_EDGE",EDGE,{"disambiguationData":[OSD([sQuery(id+"F3.wireOp",EDGE,"E12.MirrorCS")])],"isStart":true});
            fillet(context, id + "F39", {"entities" : qUnion([Q0, Q1, Q2, Q3, Q4, Q5, Q6, Q7, Q8, Q9, Q10, Q11, Q12, Q13, Q14, Q15, Q16, Q17, Q18, Q19]), "radius" : 3.75 * mm, "tangentPropagation" : true, "allowEdgeOverflow" : false});
        }
        {
            var Q0;
            Q0=qCreatedBy(id+"F22.planeOp",FACE);
            var sketch = newSketch(context, id + "F40", { "sketchPlane" : qUnion([Q0])});
            skLineSegment(sketch, "E165.top", {"start": v(210, -41.16) * mm, "end": v(157.5, -41.16) * mm});
            skLineSegment(sketch, "E165.left", {"start": v(210, 5) * mm, "end": v(210, -41.16) * mm});
            skLineSegment(sketch, "E165.right", {"start": v(157.5, 5) * mm, "end": v(157.5, -41.16) * mm});
            skLineSegment(sketch, "E166.0", {"start": v(210, 5) * mm, "end": v(157.5, 5) * mm});
            skSolve(sketch);
        }
        {
            var Q0;
            Q0 = qSketchRegion(id + "F40", true);
            extrude(context, id + "F41", {"entities" : qUnion([Q0]), "oppositeDirection" : true, "depth" : 25 * mm, "offsetDistance" : 25 * mm, "hasSecondDirection" : true, "secondDirectionOppositeDirection" : false, "secondDirectionDepth" : 0.1 * mm});
        }
    });
